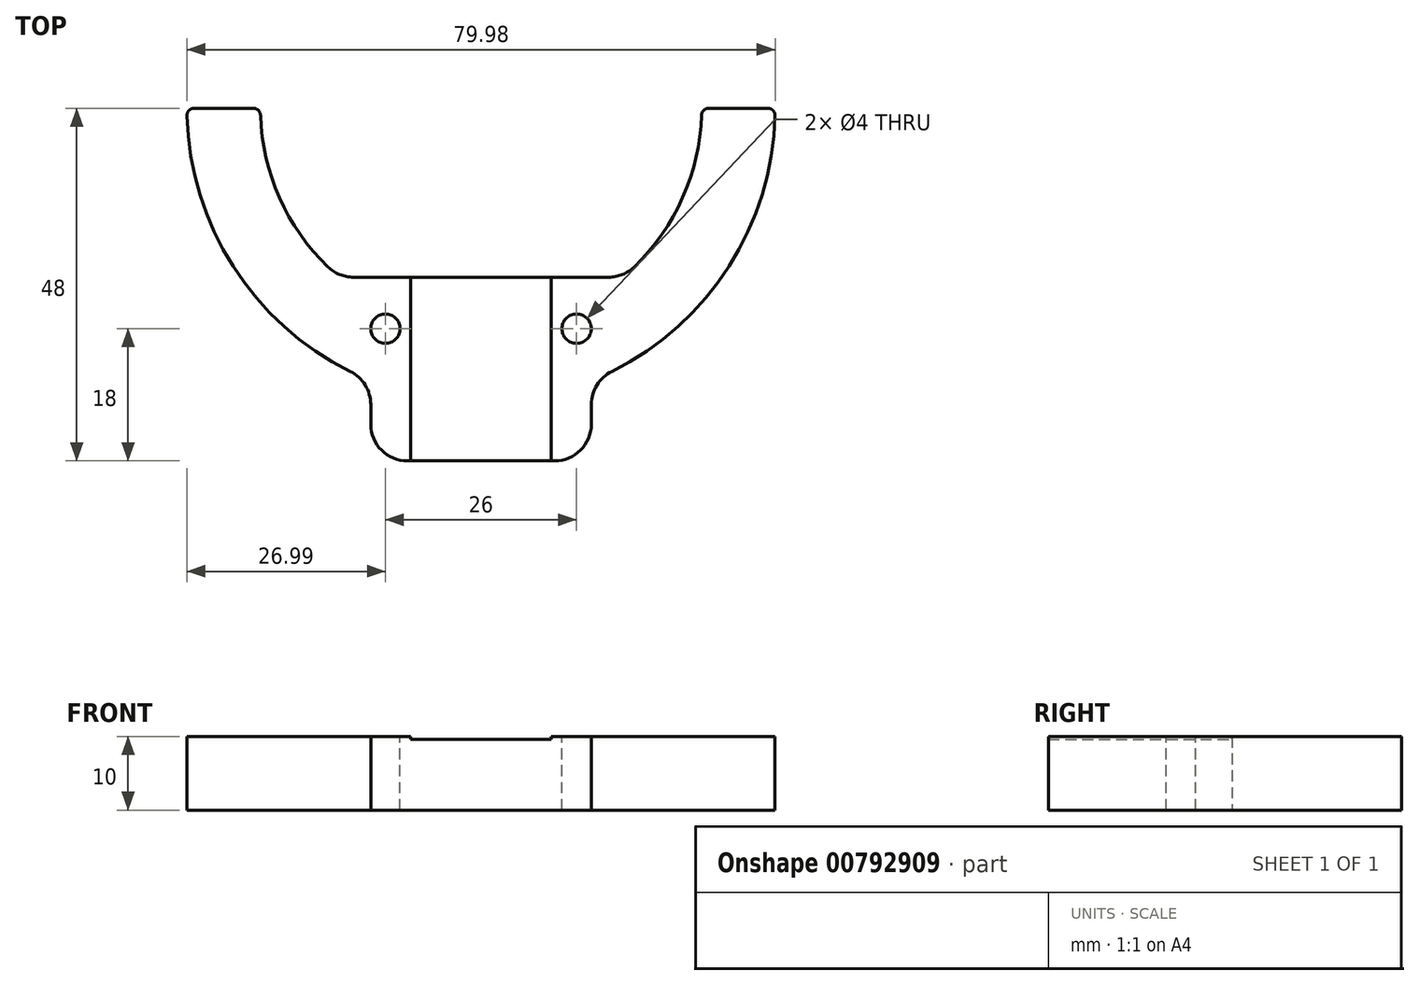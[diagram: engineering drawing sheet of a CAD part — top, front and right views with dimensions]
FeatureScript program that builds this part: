
annotation { "Feature Type Name" : "Feature", "Feature Type Description" : "" }
export const myFeature = defineFeature(function(context is Context, id is Id, definition is map)
    precondition{}
    {
        {
            var Q0;
            Q0=qCreatedBy(makeId("Top.planeOp"),FACE);
            var sketch = newSketch(context, id + "F0", { "sketchPlane" : qUnion([Q0])});
            skArc(sketch, "E0", {"start": v(-40, 0) * mm, "mid": v(-33.17, -22.36) * mm, "end": v(-15, -37.08) * mm});
            skArc(sketch, "E1", {"start": v(-30, 0) * mm, "mid": v(-27.18, -12.7) * mm, "end": v(-19.26, -23) * mm});
            skLineSegment(sketch, "E2", {"start": v(-40, 0) * mm, "end": v(-30, 0) * mm});
            skLineSegment(sketch, "E3.trimOffspring", {"start": v(30, 0) * mm, "end": v(40, 0) * mm});
            skLineSegment(sketch, "E4.bottom", {"start": v(19.26, -23) * mm, "end": v(-19.26, -23) * mm});
            skLineSegment(sketch, "E4.top", {"start": v(15, -48) * mm, "end": v(-15, -48) * mm});
            skPoint(sketch, "E4.middle", {"position": v(0, -35.5) * mm});
            skPoint(sketch, "E4.middle.positionSnap0", {"position": v(0, -30) * mm});
            skPoint(sketch, "E4.centerSnap0", {"position": v(0, -30) * mm});
            skArc(sketch, "E5.trimOffspring", {"start": v(19.26, -23) * mm, "mid": v(27.18, -12.7) * mm, "end": v(30, 0) * mm});
            skArc(sketch, "E6.trimOffspring", {"start": v(15, -37.08) * mm, "mid": v(33.17, -22.36) * mm, "end": v(40, 0) * mm});
            skLineSegment(sketch, "E7.trimOffspring", {"start": v(-15, -37.08) * mm, "end": v(-15, -48) * mm});
            skLineSegment(sketch, "E8.trimOffspring", {"start": v(15, -37.08) * mm, "end": v(15, -48) * mm});
            skPoint(sketch, "E9.orphan", {"position": v(-15, -23) * mm});
            skPoint(sketch, "E10.orphan", {"position": v(15, -23) * mm});
            skSolve(sketch);
        }
        {
            var Q0;
            Q0 = qSketchRegion(id + "F0", true);
            extrude(context, id + "F1", {"entities" : qUnion([Q0]), "depth" : 10 * mm, "offsetDistance" : 25 * mm});
        }
        {
            var Q0;
            Q0=makeQuery(id+"F1.opExtrude","CAP_FACE",FACE,{"disambiguationData":[OSD([sQuery(id+"F0.wireOp",EDGE,"E0"),sQuery(id+"F0.wireOp",EDGE,"E1"),sQuery(id+"F0.wireOp",EDGE,"E2"),sQuery(id+"F0.wireOp",EDGE,"E3.trimOffspring"),sQuery(id+"F0.wireOp",EDGE,"E4.bottom"),sQuery(id+"F0.wireOp",EDGE,"E4.top"),sQuery(id+"F0.wireOp",EDGE,"E5.trimOffspring"),sQuery(id+"F0.wireOp",EDGE,"E6.trimOffspring"),sQuery(id+"F0.wireOp",EDGE,"E7.trimOffspring"),sQuery(id+"F0.wireOp",EDGE,"E8.trimOffspring")])],"isStart":false});
            var sketch = newSketch(context, id + "F2", { "sketchPlane" : qUnion([Q0])});
            skLineSegment(sketch, "E11.bottom", {"start": v(-9.55, -48) * mm, "end": v(9.55, -48) * mm});
            skLineSegment(sketch, "E11.top", {"start": v(-9.55, -23) * mm, "end": v(9.55, -23) * mm});
            skLineSegment(sketch, "E11.left", {"start": v(-9.55, -48) * mm, "end": v(-9.55, -23) * mm});
            skLineSegment(sketch, "E11.right", {"start": v(9.55, -48) * mm, "end": v(9.55, -23) * mm});
            skSolve(sketch);
        }
        {
            var Q0;
            Q0 = qSketchRegion(id + "F2", true);
            extrude(context, id + "F3", {"entities" : qUnion([Q0]), "operationType" : NewBodyOperationType.REMOVE, "oppositeDirection" : true, "depth" : .4 * mm, "offsetDistance" : 25 * mm});
        }
        {
            var Q0;
            {var subQ0=sQuery(id+"F0.wireOp",EDGE,"E4.bottom");var subQ1=sQuery(id+"F0.wireOp",EDGE,"E2");var subQ2=sQuery(id+"F0.wireOp",EDGE,"E1");var subQ3=sQuery(id+"F0.wireOp",EDGE,"E0");var subQ4=sQuery(id+"F0.wireOp",EDGE,"E4.top");var subQ5=sQuery(id+"F0.wireOp",EDGE,"E7.trimOffspring");Q0=makeQuery(id+"F3.boolean.opBoolean","SPLIT",FACE,{"disambiguationData":[TD([makeQuery(id+"F1.opExtrude","SWEPT_FACE",FACE,{"disambiguationData":[OSD([subQ3])]})])],"derivedFrom":makeQuery(id+"F1.opExtrude","CAP_FACE",FACE,{"disambiguationData":[OSD([subQ3,subQ2,subQ1,sQuery(id+"F0.wireOp",EDGE,"E3.trimOffspring"),subQ0,subQ4,sQuery(id+"F0.wireOp",EDGE,"E5.trimOffspring"),sQuery(id+"F0.wireOp",EDGE,"E6.trimOffspring"),subQ5,sQuery(id+"F0.wireOp",EDGE,"E8.trimOffspring")])],"isStart":false})});}
            var sketch = newSketch(context, id + "F4", { "sketchPlane" : qUnion([Q0])});
            skCircle(sketch, "E12", {"center": v(-13, -30) * mm, "radius": 2 * mm});
            skPoint(sketch, "E12.centerSnap0", {"position": v(-13, -23.83) * mm});
            skCircle(sketch, "E13.MirrorC", {"center": v(13, -30) * mm, "radius": 2 * mm});
            skSolve(sketch);
        }
        {
            var Q0;
            Q0 = qSketchRegion(id + "F4", true);
            extrude(context, id + "F5", {"entities" : qUnion([Q0]), "operationType" : NewBodyOperationType.REMOVE, "endBound" : BoundingType.THROUGH_ALL, "oppositeDirection" : true, "depth" : 25 * mm, "offsetDistance" : 25 * mm});
        }
        {
            var Q0;
            Q0=makeQuery(id+"F1.opExtrude","SWEPT_EDGE",EDGE,{"disambiguationData":[OSD([sQuery(id+"F0.wireOp",EDGE,"E1"),sQuery(id+"F0.wireOp",EDGE,"E4.bottom")])]});
            var Q1;
            Q1=makeQuery(id+"F1.opExtrude","SWEPT_EDGE",EDGE,{"disambiguationData":[OSD([sQuery(id+"F0.wireOp",EDGE,"E4.bottom"),sQuery(id+"F0.wireOp",EDGE,"E5.trimOffspring")])]});
            var Q2;
            Q2=makeQuery(id+"F1.opExtrude","SWEPT_EDGE",EDGE,{"disambiguationData":[OSD([sQuery(id+"F0.wireOp",EDGE,"E6.trimOffspring"),sQuery(id+"F0.wireOp",EDGE,"E8.trimOffspring")])]});
            var Q3;
            Q3=makeQuery(id+"F1.opExtrude","SWEPT_EDGE",EDGE,{"disambiguationData":[OSD([sQuery(id+"F0.wireOp",EDGE,"E0"),sQuery(id+"F0.wireOp",EDGE,"E7.trimOffspring")])]});
            var Q4;
            Q4=makeQuery(id+"F1.opExtrude","SWEPT_EDGE",EDGE,{"disambiguationData":[OSD([sQuery(id+"F0.wireOp",EDGE,"E4.top"),sQuery(id+"F0.wireOp",EDGE,"E7.trimOffspring")])]});
            var Q5;
            Q5=makeQuery(id+"F1.opExtrude","SWEPT_EDGE",EDGE,{"disambiguationData":[OSD([sQuery(id+"F0.wireOp",EDGE,"E4.top"),sQuery(id+"F0.wireOp",EDGE,"E8.trimOffspring")])]});
            fillet(context, id + "F6", {"entities" : qUnion([Q0, Q1, Q2, Q3, Q4, Q5]), "radius" : 5 * mm, "tangentPropagation" : true, "allowEdgeOverflow" : false});
        }
        {
            var Q0;
            Q0=makeQuery(id+"F1.opExtrude","SWEPT_EDGE",EDGE,{"disambiguationData":[OSD([sQuery(id+"F0.wireOp",EDGE,"E0"),sQuery(id+"F0.wireOp",EDGE,"E2")])]});
            var Q1;
            Q1=makeQuery(id+"F1.opExtrude","SWEPT_EDGE",EDGE,{"disambiguationData":[OSD([sQuery(id+"F0.wireOp",EDGE,"E1"),sQuery(id+"F0.wireOp",EDGE,"E2")])]});
            var Q2;
            Q2=makeQuery(id+"F1.opExtrude","SWEPT_EDGE",EDGE,{"disambiguationData":[OSD([sQuery(id+"F0.wireOp",EDGE,"E3.trimOffspring"),sQuery(id+"F0.wireOp",EDGE,"E5.trimOffspring")])]});
            var Q3;
            Q3=makeQuery(id+"F1.opExtrude","SWEPT_EDGE",EDGE,{"disambiguationData":[OSD([sQuery(id+"F0.wireOp",EDGE,"E3.trimOffspring"),sQuery(id+"F0.wireOp",EDGE,"E6.trimOffspring")])]});
            fillet(context, id + "F7", {"entities" : qUnion([Q0, Q1, Q2, Q3]), "radius" : 1 * mm, "tangentPropagation" : true, "allowEdgeOverflow" : false});
        }
    });
